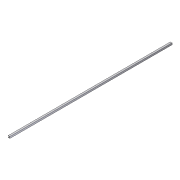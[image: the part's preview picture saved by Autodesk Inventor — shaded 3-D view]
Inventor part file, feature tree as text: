
AUTODESK INVENTOR PART (.ipt)
format: ipt  version: 2012 (Build 160160000, 160)  size: 71,168 bytes
history: native  units: in
note: dims shown in document units (in); Inventor stores cm internally (conversion verified against a paired STEP export)
features: extrude x1, sketch x1
ambient origin geometry x8: Origin, YZ Plane, XZ Plane, XY Plane, X Axis, Y Axis, Z Axis, Center Point
bodies: Solid1 (feature_tree)
feature tree (2):
  extrude  "Extrusion1"  Depth=0.75in
  sketch  "Sketch1"  dims[d0=0.75in d1=0.75in d2=0.125in d3=0.125in d4=0.125in d5=72.0in d6=0.0in]
